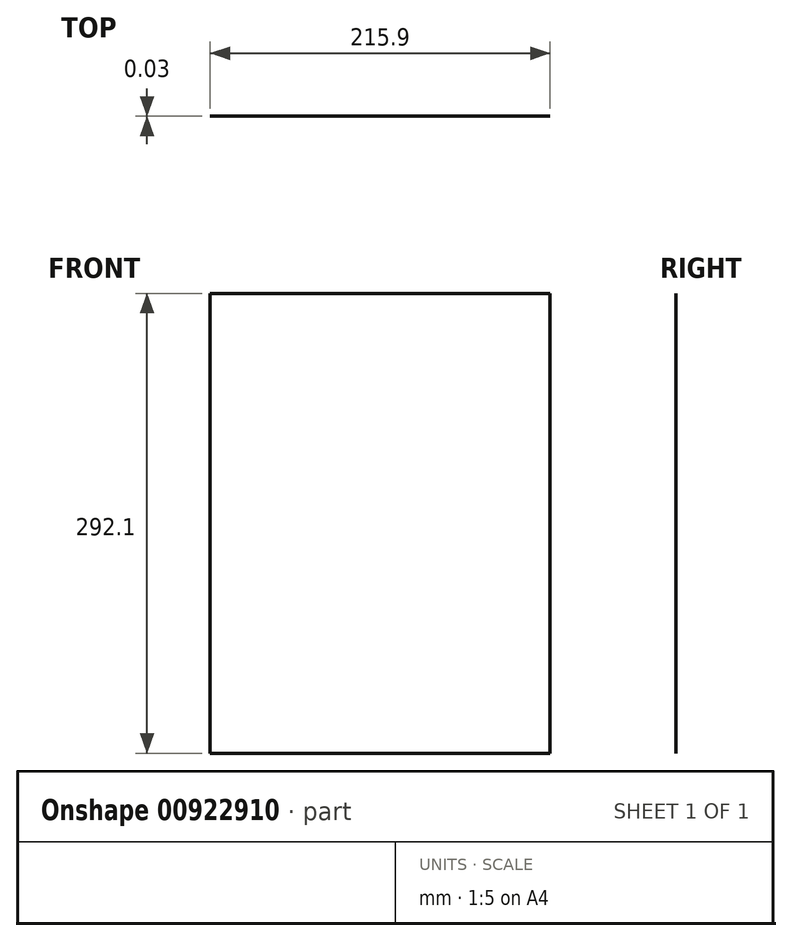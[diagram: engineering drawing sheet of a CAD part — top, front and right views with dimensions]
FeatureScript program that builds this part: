
annotation { "Feature Type Name" : "Feature", "Feature Type Description" : "" }
export const myFeature = defineFeature(function(context is Context, id is Id, definition is map)
    precondition{}
    {
        {
            var Q0;
            Q0=qCreatedBy(makeId("Front.planeOp"),FACE);
            var sketch = newSketch(context, id + "F0", { "sketchPlane" : qUnion([Q0])});
            skLineSegment(sketch, "E0.bottom", {"start": v(-152.22, 148.77) * mm, "end": v(63.68, 148.77) * mm});
            skLineSegment(sketch, "E0.top", {"start": v(-152.22, -143.33) * mm, "end": v(63.68, -143.33) * mm});
            skLineSegment(sketch, "E0.left", {"start": v(-152.22, 148.77) * mm, "end": v(-152.22, -143.33) * mm});
            skLineSegment(sketch, "E0.right", {"start": v(63.68, 148.77) * mm, "end": v(63.68, -143.33) * mm});
            skSolve(sketch);
        }
        {
            var Q0;
            Q0 = qSketchRegion(id + "F0", true);
            extrude(context, id + "F1", {"entities" : qUnion([Q0]), "depth" : 0.03 * mm, "offsetDistance" : 25.4 * mm});
        }
    });
